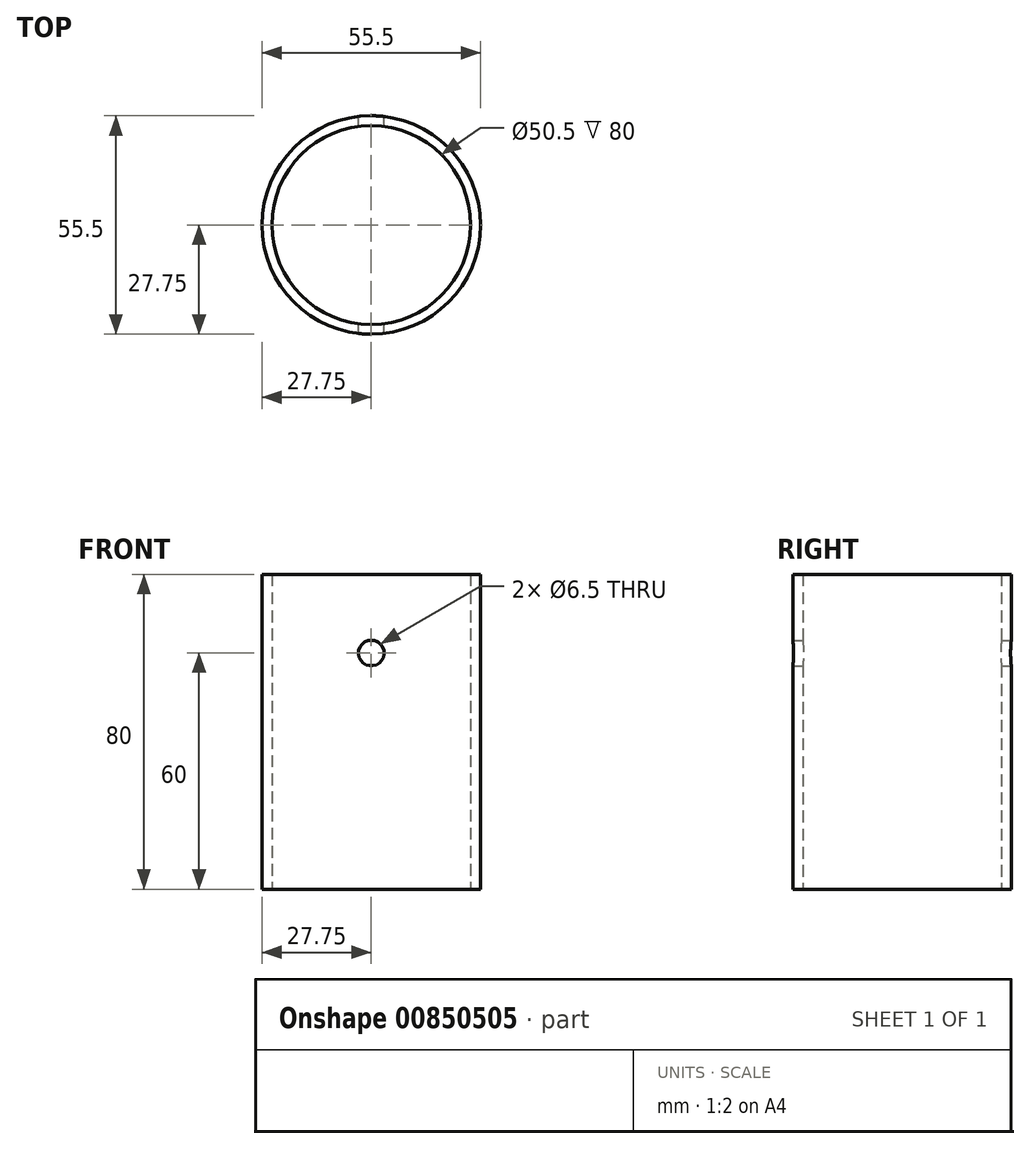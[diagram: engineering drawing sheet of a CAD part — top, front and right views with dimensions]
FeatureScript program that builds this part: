
annotation { "Feature Type Name" : "Feature", "Feature Type Description" : "" }
export const myFeature = defineFeature(function(context is Context, id is Id, definition is map)
    precondition{}
    {
        {
            var Q0;
            Q0=qCreatedBy(makeId("Top.planeOp"),FACE);
            var sketch = newSketch(context, id + "F0", { "sketchPlane" : qUnion([Q0])});
            skCircle(sketch, "E0", {"center": v(0, 0) * mm, "radius": 27.75 * mm});
            skSolve(sketch);
        }
        {
            var Q0;
            Q0=makeQuery(id+"F0.imprint","IMPRINT",FACE,{"disambiguationData":[TD([[makeQuery(id+"F0.imprint","IMPRINT",EDGE,{"derivedFrom":sQuery(id+"F0.wireOp",EDGE,"E0")}),1.0]])]});
            var Q1;
            Q1=sQuery(id+"F0.wireOp",EDGE,"E0");
            extrude(context, id + "F1", {"entities" : qUnion([Q0]), "surfaceEntities" : qUnion([Q1]), "depth" : 80 * mm, "offsetDistance" : 25 * mm});
        }
        {
            var Q0;
            Q0=makeQuery(id+"F1.opExtrude","CAP_FACE",FACE,{"disambiguationData":[OSD([sQuery(id+"F0.wireOp",EDGE,"E0")])],"isStart":false});
            var Q1;
            Q1=makeQuery(id+"F1.opExtrude","CAP_FACE",FACE,{"disambiguationData":[OSD([sQuery(id+"F0.wireOp",EDGE,"E0")])],"isStart":true});
            shell(context, id + "F2", {"entities" : qUnion([Q0, Q1]), "thickness" : 2.5 * mm});
        }
        {
            var Q0;
            Q0=qCreatedBy(makeId("Front.planeOp"),FACE);
            var sketch = newSketch(context, id + "F3", { "sketchPlane" : qUnion([Q0])});
            skCircle(sketch, "E1", {"center": v(0, 60) * mm, "radius": 3.25 * mm});
            skSolve(sketch);
        }
        {
            var Q0;
            Q0 = qSketchRegion(id + "F3", true);
            extrude(context, id + "F4", {"entities" : qUnion([Q0]), "operationType" : NewBodyOperationType.REMOVE, "depth" : 60 * mm, "offsetDistance" : 25 * mm, "symmetric" : true});
        }
    });
